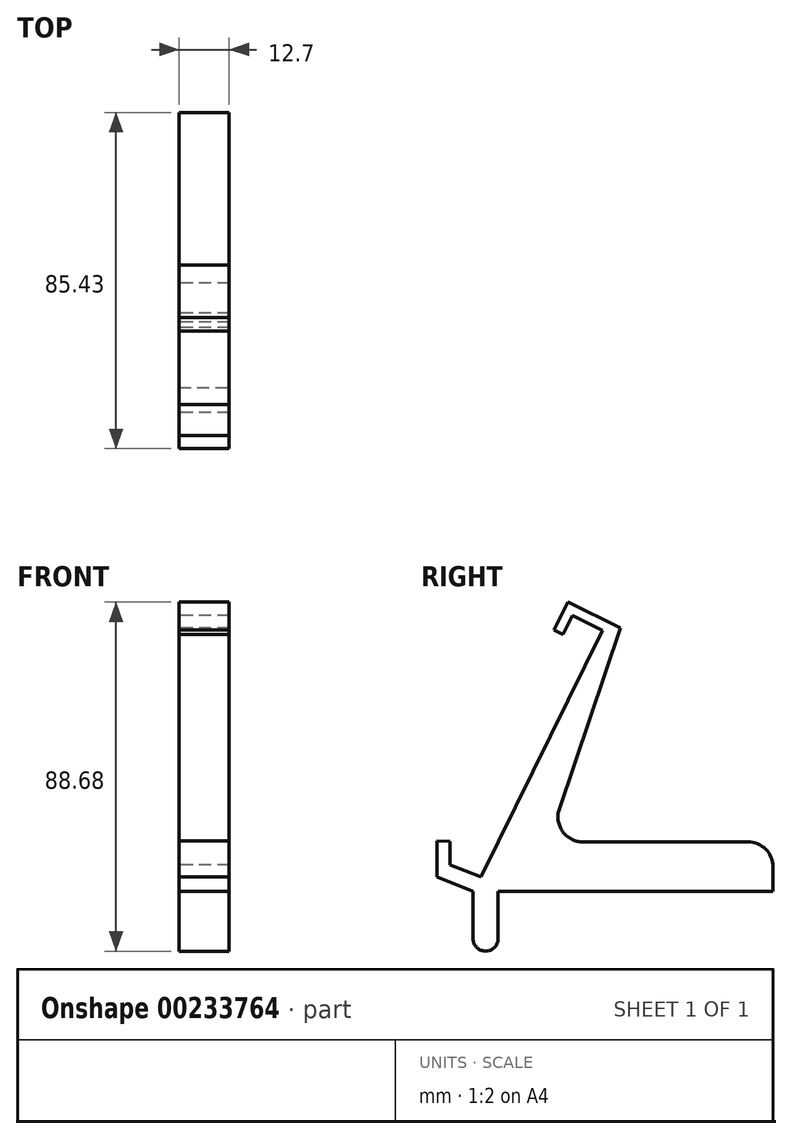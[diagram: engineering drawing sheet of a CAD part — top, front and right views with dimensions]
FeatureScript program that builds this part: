
annotation { "Feature Type Name" : "Feature", "Feature Type Description" : "" }
export const myFeature = defineFeature(function(context is Context, id is Id, definition is map)
    precondition{}
    {
        {
            var Q0;
            Q0=qCreatedBy(makeId("Right.planeOp"),FACE);
            var sketch = newSketch(context, id + "F0", { "sketchPlane" : qUnion([Q0])});
            skLineSegment(sketch, "E0", {"start": v(0, 0) * mm, "end": v(0, 30.48) * mm});
            skLineSegment(sketch, "E1", {"start": v(0, 30.48) * mm, "end": v(-254, 30.48) * mm});
            skLineSegment(sketch, "E2", {"start": v(-254, 30.48) * mm, "end": v(-263.23, 34.18) * mm});
            skLineSegment(sketch, "E3", {"start": v(-263.23, 34.18) * mm, "end": v(-263.23, 43.27) * mm});
            skLineSegment(sketch, "E4", {"start": v(-263.23, 43.27) * mm, "end": v(-259.91, 43.18) * mm});
            skLineSegment(sketch, "E5", {"start": v(-259.91, 43.18) * mm, "end": v(-259.91, 37.23) * mm});
            skLineSegment(sketch, "E6", {"start": v(-259.91, 37.23) * mm, "end": v(-251.99, 34.05) * mm});
            skLineSegment(sketch, "E7", {"start": v(-251.99, 34.05) * mm, "end": v(-221.14, 96.72) * mm});
            skLineSegment(sketch, "E8", {"start": v(-221.14, 96.72) * mm, "end": v(-228.78, 100.48) * mm});
            skLineSegment(sketch, "E9", {"start": v(-228.78, 100.48) * mm, "end": v(-231.13, 95.71) * mm});
            skLineSegment(sketch, "E10", {"start": v(-231.13, 95.71) * mm, "end": v(-233.4, 96.84) * mm});
            skLineSegment(sketch, "E11", {"start": v(-233.4, 96.84) * mm, "end": v(-229.92, 103.92) * mm});
            skLineSegment(sketch, "E12", {"start": v(-229.92, 103.92) * mm, "end": v(-208.15, 93.21) * mm});
            skLineSegment(sketch, "E13", {"start": v(-216.56, 97.35) * mm, "end": v(-208.15, 93.21) * mm});
            skLineSegment(sketch, "E14", {"start": v(-216.56, 97.35) * mm, "end": v(-232.12, 51.39) * mm});
            skLineSegment(sketch, "E15", {"start": v(-226.1, 43) * mm, "end": v(-184.15, 43) * mm});
            skLineSegment(sketch, "E16", {"start": v(-177.8, 36.65) * mm, "end": v(-177.8, 30.48) * mm});
            skPoint(sketch, "E17.visualSharp", {"position": v(-234.96, 43) * mm});
            skArc(sketch, "E17.filletArc", {"start": v(-232.12, 51.39) * mm, "mid": v(-231.26, 45.65) * mm, "end": v(-226.1, 43) * mm});
            skPoint(sketch, "E18.visualSharp", {"position": v(-177.8, 43) * mm});
            skArc(sketch, "E18.filletArc", {"start": v(-177.8, 36.65) * mm, "mid": v(-179.66, 41.14) * mm, "end": v(-184.15, 43) * mm});
            skSolve(sketch);
        }
        {
            var Q0;
            Q0 = qSketchRegion(id + "F0", true);
            extrude(context, id + "F1", {"entities" : qUnion([Q0]), "depth" : 12.7 * mm});
        }
        {
            var Q0;
            Q0=makeQuery(id+"F1.opExtrude","CAP_FACE",FACE,{"disambiguationData":[OSD([sQuery(id+"F0.wireOp",EDGE,"E1"),sQuery(id+"F0.wireOp",EDGE,"E2"),sQuery(id+"F0.wireOp",EDGE,"E3"),sQuery(id+"F0.wireOp",EDGE,"E4"),sQuery(id+"F0.wireOp",EDGE,"E5"),sQuery(id+"F0.wireOp",EDGE,"E6"),sQuery(id+"F0.wireOp",EDGE,"E7"),sQuery(id+"F0.wireOp",EDGE,"E8"),sQuery(id+"F0.wireOp",EDGE,"E9"),sQuery(id+"F0.wireOp",EDGE,"E10"),sQuery(id+"F0.wireOp",EDGE,"E11"),sQuery(id+"F0.wireOp",EDGE,"E12"),sQuery(id+"F0.wireOp",EDGE,"E14"),sQuery(id+"F0.wireOp",EDGE,"E15"),sQuery(id+"F0.wireOp",EDGE,"E16"),sQuery(id+"F0.wireOp",EDGE,"E17.filletArc"),sQuery(id+"F0.wireOp",EDGE,"E18.filletArc")])],"isStart":false});
            var sketch = newSketch(context, id + "F2", { "sketchPlane" : qUnion([Q0])});
            skLineSegment(sketch, "E19.bottom", {"start": v(-254, 30.48) * mm, "end": v(-247.65, 30.48) * mm});
            skLineSegment(sketch, "E19.top", {"start": v(-250.83, 15.24) * mm, "end": v(-250.83, 15.24) * mm});
            skLineSegment(sketch, "E19.left", {"start": v(-254, 30.48) * mm, "end": v(-254, 18.42) * mm});
            skLineSegment(sketch, "E19.right", {"start": v(-247.65, 30.48) * mm, "end": v(-247.65, 18.42) * mm});
            skPoint(sketch, "E20.visualSharp", {"position": v(-247.65, 15.24) * mm});
            skArc(sketch, "E20.filletArc", {"start": v(-250.83, 15.24) * mm, "mid": v(-248.58, 16.17) * mm, "end": v(-247.65, 18.42) * mm});
            skPoint(sketch, "E21.visualSharp", {"position": v(-254, 15.24) * mm});
            skArc(sketch, "E21.filletArc", {"start": v(-254, 18.42) * mm, "mid": v(-253.07, 16.17) * mm, "end": v(-250.83, 15.24) * mm});
            skSolve(sketch);
        }
        {
            var Q0;
            Q0 = qSketchRegion(id + "F2", true);
            extrude(context, id + "F3", {"entities" : qUnion([Q0]), "operationType" : NewBodyOperationType.ADD, "oppositeDirection" : true, "depth" : 12.7 * mm});
        }
    });
